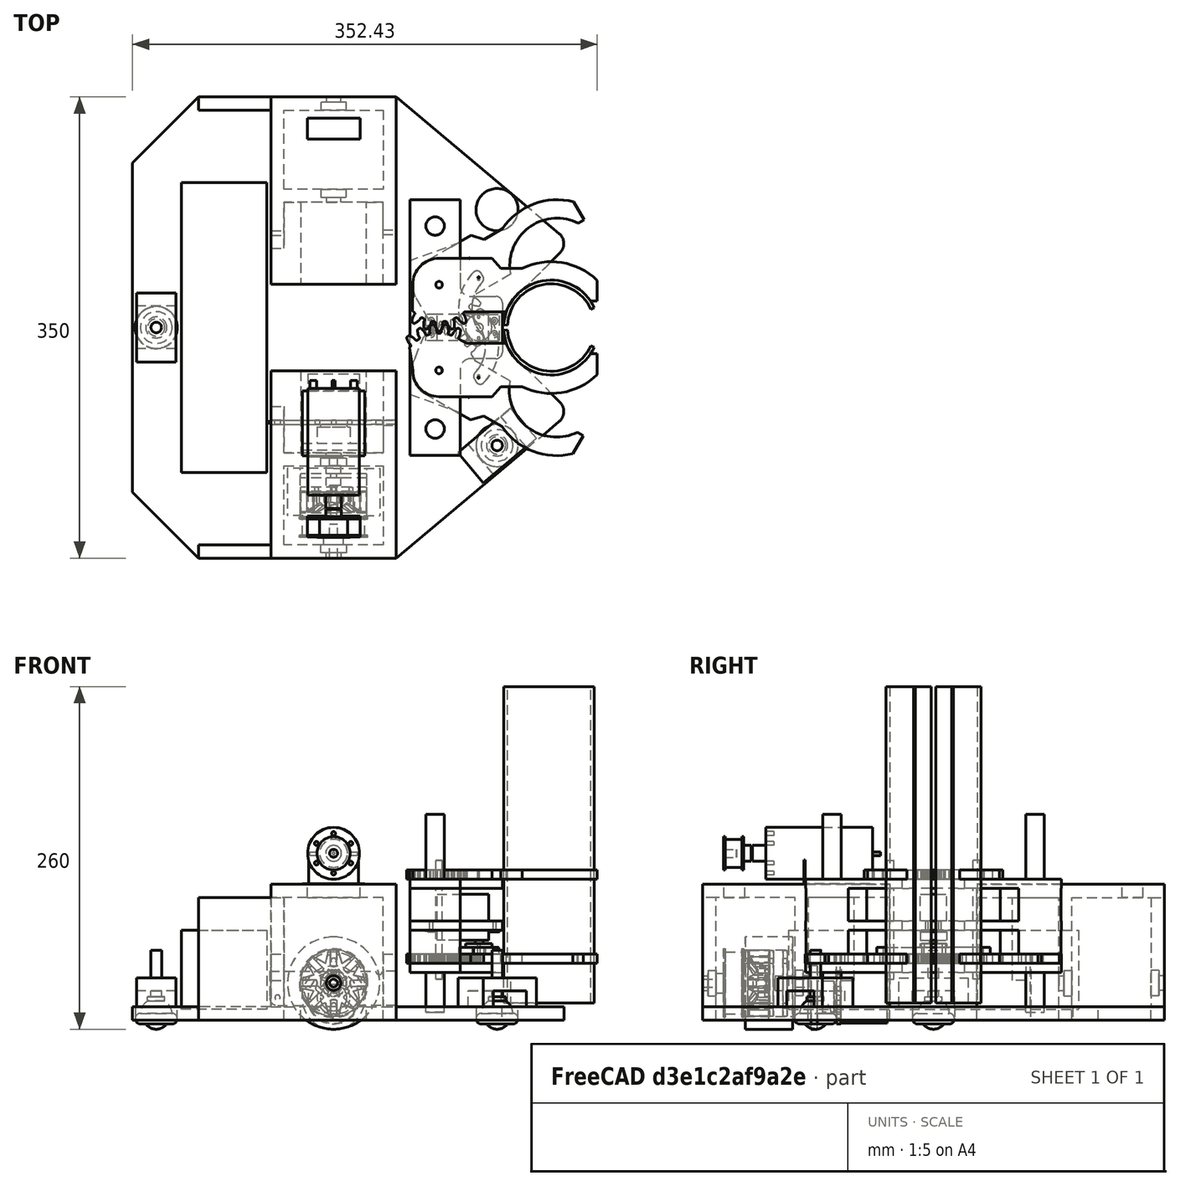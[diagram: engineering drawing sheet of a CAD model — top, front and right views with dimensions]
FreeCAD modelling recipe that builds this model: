
FCSTD DOCUMENT  (FreeCAD 0.15R4669 (Git))
Label: BR_assemblage
License: All rights reserved
LicenseURL: http://en.wikipedia.org/wiki/All_rights_reserved
objects: Part::Feature×7, Part::MultiFuse×4, Part::Mirroring×4, Part::Revolution×2, Part::Extrusion×1, Part::FeaturePython×1
note: 19 computed .brp shape members not serialized (recipe doc carries the construction recipe); baked Part::Feature solids carry a one-line shape summary decoded from their .brp

FEATURE [Part::Revolution] Revolve  label="codeur"
  Angle = 360
  Axis = (0,1,0)
  Base = (0,0,0)
  Placement = pos=(0,64,19) rot=(0,0,1;3.14159rad)
  Solid = true
FEATURE [Part::Feature] Extrude  label="batterie"
  Placement = pos=(-83,-110,40) rot=(0,0,1;0rad)
  shape: bbox 65 x 220 x 60 mm, 6 faces (baked)
FEATURE [Part::MultiFuse] Fusion006  label="Pince"
  Placement = pos=(80,0,45) rot=(0,0,-1;1.5708rad)
FEATURE [Part::Feature] Fusion007  label="moteur"
  Placement = pos=(0,97.2,128.5) rot=(0,0,1;1.5708rad)
  shape: bbox 47 x 119.1 x 43.15 mm, 62 faces, 2 solids (baked)
FEATURE [Part::Mirroring] Part__Mirroring002  label="moteur (Mirror #3)"
  Base = (0,0,0)
  Normal = (0,1,0)
  Source = -> Fusion007
FEATURE [Part::Feature] Fusion  label="assemblageRoue"
  Placement = pos=(0,132.8,30) rot=(0,0,1;0rad)
  shape: bbox 70 x 80 x 70 mm, 151 faces, 2 solids (baked)
FEATURE [Part::Mirroring] Part__Mirroring003  label="assemblageRoue (Mirror #3)"
  Base = (0,0,0)
  Normal = (0,1,0)
  Source = -> Fusion
FEATURE [Part::Feature] Extrude001  label="supportCodeur"
  Placement = pos=(0,70.4,19) rot=(0,0,1;0rad)
  shape: bbox 96 x 3 x 40 mm, 18 faces (baked)
FEATURE [Part::MultiFuse] Fusion008  label="ensembleCodeur"
  Shapes = -> [Revolve,Extrude001]
FEATURE [Part::Mirroring] Part__Mirroring  label="ensembleCodeur (Mirror #3)"
  Base = (0,0,0)
  Normal = (0,1,0)
  Source = -> Fusion008
FEATURE [Part::Revolution] Revolve001  label="billePorteuse"
  Angle = 360
  Axis = (0,0,1)
  Base = (0,0,1)
  Solid = true
FEATURE [Part::Feature] Cut  label="pince_g_servo open"
  Placement = pos=(-4.5,16.5,0) rot=(0,0,1;0.523599rad)
  shape: bbox 99.39 x 130.1 x 7 mm, 56 faces (baked)
FEATURE [Part::Feature] Cut001  label="pince_d_servo open"
  Placement = pos=(4.68911,16,0) rot=(0,0,-1;0.523599rad)
  shape: bbox 99.39 x 130.1 x 7 mm, 58 faces (baked)
FEATURE [Part::MultiFuse] Fusion010  label="PincesOuvertes"
  Placement = pos=(79.5,0,45) rot=(0,0,-1;1.5708rad)
  Shapes = -> [Cut001,Cut]
FEATURE [Part::Extrusion] Extrude002  label="archeBillePorteuse"
  Dir = (0,30,0)
  Placement = pos=(0,-15,17) rot=(0,0,1;0rad)
  Solid = true
FEATURE [Part::MultiFuse] Fusion011  label="ensembleBillePorteuse"
  Placement = pos=(124,89.5,-5) rot=(0,0,1;2.44346rad)
  Shapes = -> [Extrude002,Revolve001]
FEATURE [Part::FeaturePython] Clone  label="Clone of ensembleBillePorteuse"  # Draft clone (typed FeaturePython)
  Objects = -> [Fusion011]
  Placement = pos=(-134.5,0,-5) rot=(0,0,1;1.5708rad)
  Scale = (1,1,1)
FEATURE [Part::Mirroring] Part__Mirroring004  label="ensembleBillePorteuse (Mirror #4)"
  Base = (0,0,0)
  Normal = (0,1,0)
  Source = -> Fusion011
FEATURE [Part::Feature] Fusion009  label="baseRoulante"
  Placement = pos=(0,0,30) rot=(0,0,1;0rad)
  shape: bbox 327.1 x 350 x 103 mm, 113 faces (baked)
